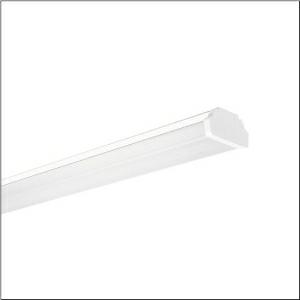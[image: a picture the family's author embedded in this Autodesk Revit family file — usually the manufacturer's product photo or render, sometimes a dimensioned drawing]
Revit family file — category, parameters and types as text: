
# Revit family: dus_r__31_gen_2_53bd813dv4a5c2_df10
name_source: partatom
category: Lighting Fixtures
units: mm (PartAtom-declared; Revit-internal decimal feet)

## family parameters
Cut with Voids When Loaded = No
Host = Face
Light Source = No
Part Type = Normal
Room Calculation Point = No
Round Connector Dimension = Use Diameter
Shared = No

## types (1)
- --- (1 x LED, 10610 lm, 61.4 W, 4000K)
    Apparent Load = 61 VA
    CIE Flux Codes = 62 83 95 93 100
    Color Rendering = 80
    Color Temperature = 4000K
    Default Elevation = 1800 mm
    Description = DUS® 31 Gen.2, luminaire insert, of sheet steel, coil coated, white, length: 1.535mm, width: 81mm, height: 90mm, 5x system unit, system units: 307mm, LED rated luminous flux: 10.610lm, light colour: 840, control gear: DALI 2, control gear: ECG DALI, with plug, 5-pole, with phase selection, mains connection: 220..240V, AC, 50/60Hz, rated input power: 61W, through-wiring accessed according to module size, primary optical cover: cover, of PMMA, light emission: direct distribution, primary light characteristic: symmetric, protection rating (complete): IP20, protection rating (LED compartment): IP50, insulation class (complete): insulation class I (protective earthing), certification: CE, ENEC, VDE, UKCA, impact resistance: IK03, permissible ambient temperature for indoor applications: -25..+35°C, corresponds to IFS (International Featured Standards) requirements for safety and quality in the food industry, reducing of maximum allowable ambient temperature of 5°C with ceiling mounting, packaging unit: 1 piece
    Height = 95 mm
    Lamp = 1 x LED
    Lamp Light Flux = 10610 lm
    Lamp Power = 61.4 W
    Lamp count = 1
    Length = 1535 mm
    Luminous efficacy = 173 lm/W
    Manufacturer = Siteco
    ModVariant = No
    Model = 53BD813DV4A5C2
    Mounting Place = Ceiling
    Mounting Type = Pendant
    Number of Poles = 1
    OnlyDefault = Yes
    Power Factor = 1
    Product Name = DUS® 31 Gen.2
    Product group = luminaire insert
    ProductGroupID = 902
    Protection Class = Protection class I
    Protection Degree = IP 20
    RLX_Detail_Level = 1
    RLX_Emergency_Light_Flux = 0 lm
    RLX_Emergency_Type = 0
    RLX_Emergency_Type_DB = No
    RlxData = <blob elided: 32169 chars, md5=0982946e>
    Socket = socket
    Standby Power = 0 W
    System Light Flux = 10610 lm
    System Power = 61 W
    Type Comments = factory setting: luminous flux: 100 % | dim-lin: 254 | 418 mA
    Type Image = l_1319596.jpg
    URL = http://relux.com
    VarID = @adj_042916
    Voltage = 0 V
    Weight = 0.00 kg
    Width = 81 mm

## geometry (parser evidence)
native form markers: Blend x4, Sweep x13
no freeform markers — native parametric forms only
